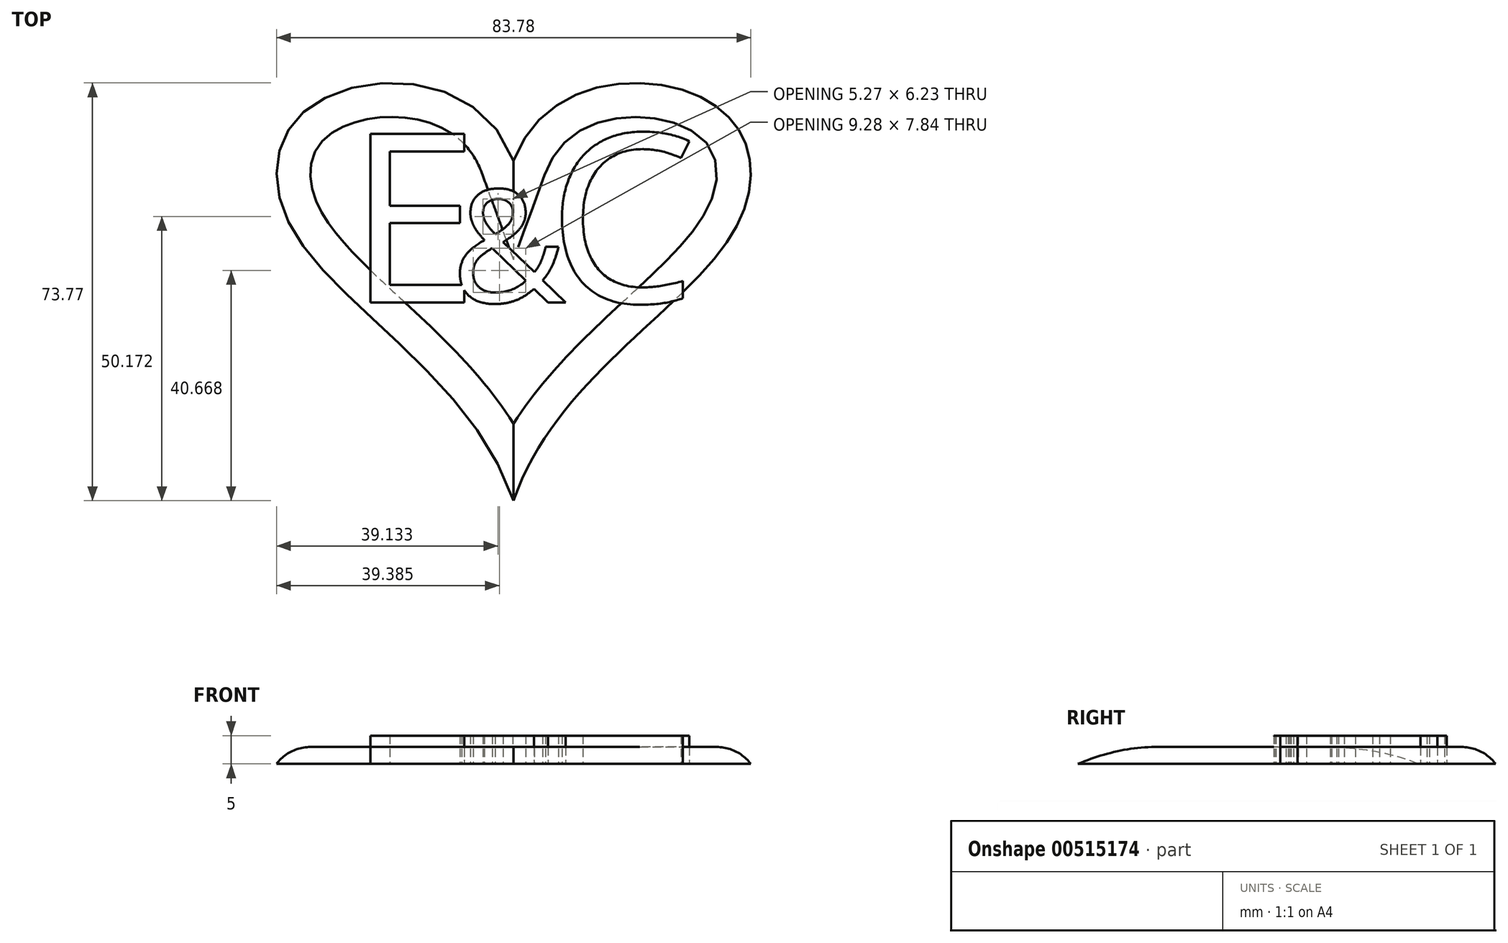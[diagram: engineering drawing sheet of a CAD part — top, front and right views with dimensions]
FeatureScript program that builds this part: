
annotation { "Feature Type Name" : "Feature", "Feature Type Description" : "" }
export const myFeature = defineFeature(function(context is Context, id is Id, definition is map)
    precondition{}
    {
        {
            var Q0;
            Q0=qCreatedBy(makeId("Top.planeOp"),FACE);
            var sketch = newSketch(context, id + "F0", { "sketchPlane" : qUnion([Q0])});
            skText(sketch, "E0", { "text": "C", "fontName": "OpenSans-Regular.ttf"});
            skText(sketch, "E1", { "text": "E", "fontName": "OpenSans-Regular.ttf"});
            skText(sketch, "E2", { "text": "&", "fontName": "OpenSans-Regular.ttf"});
            const initialGuessF0  = {"E0": [0.00601, 0, 1, 0, 0.03], "E1": [-0.02938, 0, 1, 0, 0.03], "E2": [-0.01101, 0, 1, 0, 0.02]};
            skSetInitialGuess(sketch, initialGuessF0);
            skSolve(sketch);
        }
        {
            var Q0;
            Q0=qCreatedBy(makeId("Top.planeOp"),FACE);
            var sketch = newSketch(context, id + "F1", { "sketchPlane" : qUnion([Q0])});
            skFitSpline(sketch, "E3", {"points": [v(0, 40) * mm, v(-23.44, 46.73) * mm, v(-26.04, 31.91) * mm, v(0, 0) * mm], "startDerivative": vector(-35.59, 97.15) * mm, "endDerivative": vector(35.4, -104.18) * mm});
            skFitSpline(sketch, "E4.MirrorCS", {"points": [v(0, 40) * mm, v(23.44, 46.73) * mm, v(26.04, 31.91) * mm, v(0, 0) * mm], "startDerivative": vector(35.59, 97.15) * mm, "endDerivative": vector(-35.4, -104.18) * mm});
            skSolve(sketch);
        }
        {
            var Q0;
            Q0=qSketchRegion(id+"F1",true);
            extrude(context, id + "F2", {"entities" : qUnion([Q0]), "depth" : 2 * mm});
        }
        {
            var Q0;
            Q0=makeQuery(id+"F2.opExtrude","CAP_FACE",FACE,{"disambiguationData":[OSD([sQuery(id+"F1.wireOp",EDGE,"E3"),sQuery(id+"F1.wireOp",EDGE,"E4.MirrorCS")])],"isStart":false});
            fillet(context, id + "F3", {"entities" : qUnion([Q0]), "radius" : 5 * mm, "tangentPropagation" : true, "allowEdgeOverflow" : false});
        }
        {
            var Q0;
            Q0=qSketchRegion(id+"F0",true);
            extrude(context, id + "F4", {"entities" : qUnion([Q0]), "depth" : 5 * mm});
        }
        {
            var Q0;
            Q0=makeQuery(id+"F2.opExtrude","SWEPT_BODY",BODY,{"disambiguationData":[OSD([sQuery(id+"F1.wireOp",EDGE,"E3"),sQuery(id+"F1.wireOp",EDGE,"E4.MirrorCS")])]});
            var Q1;
            Q1=qCreatedBy(makeId("Origin.pointOp"),VERTEX);
            transform(context, id + "F5", {"entities" : qUnion([Q0]), "transformType" : TransformType.SCALE_UNIFORMLY, "scale" : 1.5, "scalePoint" : qUnion([Q1]), "makeCopy" : false});
        }
        {
            var Q0;
            Q0=makeQuery(id+"F2.opExtrude","SWEPT_BODY",BODY,{"disambiguationData":[OSD([sQuery(id+"F1.wireOp",EDGE,"E3"),sQuery(id+"F1.wireOp",EDGE,"E4.MirrorCS")])]});
            var Q1;
            Q1=qCreatedBy(makeId("Origin.pointOp"),VERTEX);
            var Q2;
            Q2=qCreatedBy(makeId("Front.planeOp"),FACE);
            transform(context, id + "F6", {"entities" : qUnion([Q0]), "transformType" : TransformType.TRANSLATION_DISTANCE, "transformDirection" : qUnion([Q2]), "distance" : 35 * mm, "makeCopy" : false});
        }
    });
